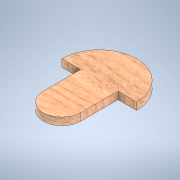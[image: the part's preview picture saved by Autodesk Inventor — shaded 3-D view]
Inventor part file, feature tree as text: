
AUTODESK INVENTOR PART (.ipt)
format: ipt  version: 2022 (Build 260153000, 153)  size: 121,856 bytes
history: native  units: mm
features: other x1, extrude x1, sketch x1
ambient origin geometry x8: Origin, YZ Plane, XZ Plane, XY Plane, X Axis, Y Axis, Z Axis, Center Point
bodies: Body1 (feature_tree)
feature tree (3):
  other  "Sólido1"
  extrude  "Extrusión1"  Depth=50.0mm
  sketch  "Boceto1"  dims[d0=100.0mm d1=50.0mm d2=100.0mm d3=10.0mm d4=0.0mm]
